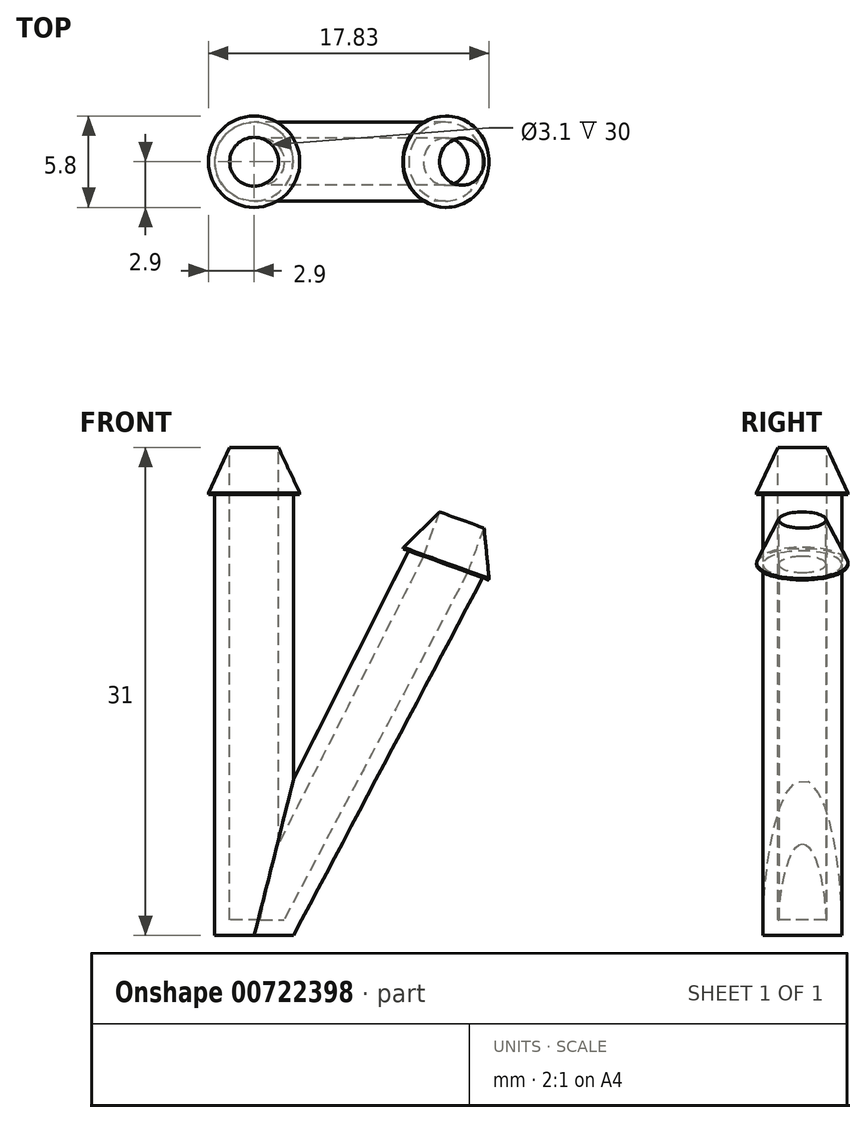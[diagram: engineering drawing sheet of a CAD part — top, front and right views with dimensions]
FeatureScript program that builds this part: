
annotation { "Feature Type Name" : "Feature", "Feature Type Description" : "" }
export const myFeature = defineFeature(function(context is Context, id is Id, definition is map)
    precondition{}
    {
        {
            var Q0;
            Q0=qCreatedBy(makeId("Top.planeOp"),FACE);
            var sketch = newSketch(context, id + "F0", { "sketchPlane" : qUnion([Q0])});
            skCircle(sketch, "E0", {"center": v(0, 0) * mm, "radius": 2.5 * mm});
            skSolve(sketch);
        }
        {
            var Q0;
            Q0=makeQuery(id+"F0.imprint","IMPRINT",FACE,{"disambiguationData":[TD([[makeQuery(id+"F0.imprint","IMPRINT",EDGE,{"derivedFrom":sQuery(id+"F0.wireOp",EDGE,"E0")}),1.0]])]});
            extrude(context, id + "F1", {"entities" : qUnion([Q0]), "depth" : 28 * mm, "offsetDistance" : 25 * mm});
        }
        {
            var Q0;
            Q0=makeQuery(id+"F1.opExtrude","CAP_FACE",FACE,{"disambiguationData":[OSD([sQuery(id+"F0.wireOp",EDGE,"E0")])],"isStart":false});
            var sketch = newSketch(context, id + "F2", { "sketchPlane" : qUnion([Q0])});
            skLineSegment(sketch, "E1", {"start": v(0, 2.5) * mm, "end": v(0, -2.5) * mm});
            skSolve(sketch);
        }
        {
            var Q0;
            Q0=sQuery(id+"F2.wireOp",EDGE,"E1");
            cPlane(context, id + "F3", {"entities" : qUnion([Q0]), "cplaneType" : CPlaneType.LINE_ANGLE, "offset" : 25 * mm, "angle" : 160 * degree, "width" : 150 * mm, "height" : 150 * mm});
        }
        {
            var Q0;
            Q0=qCreatedBy(id+"F3.planeOp",FACE);
            var sketch = newSketch(context, id + "F4", { "sketchPlane" : qUnion([Q0])});
            skCircle(sketch, "E2", {"center": v(3.37, 0) * mm, "radius": 2.5 * mm});
            skSolve(sketch);
        }
        {
            var Q1;
            Q1=makeQuery(id+"F4.imprint","IMPRINT",FACE,{"disambiguationData":[TD([[makeQuery(id+"F4.imprint","IMPRINT",EDGE,{"derivedFrom":sQuery(id+"F4.wireOp",EDGE,"E2")}),1.0]])]});
            var Q2;
            Q2=makeQuery(id+"F1.opExtrude","CAP_FACE",FACE,{"disambiguationData":[OSD([sQuery(id+"F0.wireOp",EDGE,"E0")])],"isStart":true});
            loft(context, id + "F5", {"operationType" : NewBodyOperationType.ADD, "sheetProfilesArray" : [{ "sheetProfileEntities" : qUnion([Q1]) }, { "sheetProfileEntities" : qUnion([Q2]) }]});
        }
        {
            var Q0;
            Q0=makeQuery(id+"F5.opLoft","CAP_FACE",FACE,{"disambiguationData":[OSD([makeQuery(id+"F4.imprint","IMPRINT",FACE,{"disambiguationData":[TD([[makeQuery(id+"F4.imprint","IMPRINT",EDGE,{"derivedFrom":sQuery(id+"F4.wireOp",EDGE,"E2")}),1.0]])]})])],"isStart":true});
            shell(context, id + "F6", {"entities" : qUnion([Q0]), "thickness" : 1 * mm});
        }
        {
            var Q0;
            Q0=makeQuery(id+"F1.opExtrude","CAP_FACE",FACE,{"disambiguationData":[OSD([sQuery(id+"F0.wireOp",EDGE,"E0")])],"isStart":false});
            var sketch = newSketch(context, id + "F7", { "sketchPlane" : qUnion([Q0])});
            skCircle(sketch, "E3", {"center": v(0, 0) * mm, "radius": 2.9 * mm});
            skSolve(sketch);
        }
        {
            var Q0;
            {var subQ0=sQuery(id+"F0.wireOp",EDGE,"E0");var subQ1=makeQuery(id+"F1.opExtrude","CAP_EDGE",EDGE,{"disambiguationData":[OSD([subQ0])],"isStart":false});Q0=makeQuery(id+"F7.imprint","IMPRINT",FACE,{"disambiguationData":[TD([[makeQuery(id+"F7.imprint","IMPRINT",EDGE,{"derivedFrom":subQ1}),1.0]])]});}
            cPlane(context, id + "F8", {"entities" : qUnion([Q0]), "cplaneType" : CPlaneType.OFFSET, "offset" : 3 * mm, "width" : 150 * mm, "height" : 150 * mm});
        }
        {
            var Q0;
            Q0=qCreatedBy(id+"F8.planeOp",FACE);
            var sketch = newSketch(context, id + "F9", { "sketchPlane" : qUnion([Q0])});
            skCircle(sketch, "E4", {"center": v(0, 0) * mm, "radius": 1.55 * mm});
            skSolve(sketch);
        }
        {
            var Q0;
            Q0=makeQuery(id+"F7.imprint","IMPRINT",FACE,{"disambiguationData":[TD([[makeQuery(id+"F7.imprint","IMPRINT",EDGE,{"derivedFrom":makeQuery(id+"F1.opExtrude","CAP_EDGE",EDGE,{"disambiguationData":[OSD([sQuery(id+"F0.wireOp",EDGE,"E0")])],"isStart":false})}),1.0]])]});
            var Q1;
            Q1=makeQuery(id+"F7.imprint","IMPRINT",FACE,{"disambiguationData":[TD([[makeQuery(id+"F7.imprint","IMPRINT",EDGE,{"derivedFrom":sQuery(id+"F7.wireOp",EDGE,"E3")}),1.0]])]});
            extrude(context, id + "F10", {"entities" : qUnion([Q0, Q1]), "operationType" : NewBodyOperationType.ADD, "depth" : .1 * mm, "offsetDistance" : 25 * mm});
        }
        {
            var Q1;
            Q1=makeQuery(id+"F10.opExtrude","CAP_FACE",FACE,{"disambiguationData":[OSD([sQuery(id+"F0.wireOp",EDGE,"E0"),sQuery(id+"F7.wireOp",EDGE,"E3")])],"isStart":false});
            var Q2;
            Q2=makeQuery(id+"F9.imprint","IMPRINT",FACE,{"disambiguationData":[TD([[makeQuery(id+"F9.imprint","IMPRINT",EDGE,{"derivedFrom":sQuery(id+"F9.wireOp",EDGE,"E4")}),1.0]])]});
            loft(context, id + "F11", {"operationType" : NewBodyOperationType.ADD, "sheetProfilesArray" : [{ "sheetProfileEntities" : qUnion([Q1]) }, { "sheetProfileEntities" : qUnion([Q2]) }]});
        }
        {
            var Q0;
            Q0=makeQuery(id+"F9.imprint","IMPRINT",FACE,{"disambiguationData":[TD([[makeQuery(id+"F9.imprint","IMPRINT",EDGE,{"derivedFrom":sQuery(id+"F9.wireOp",EDGE,"E4")}),1.0]])]});
            extrude(context, id + "F12", {"entities" : qUnion([Q0]), "operationType" : NewBodyOperationType.REMOVE, "oppositeDirection" : true, "depth" : 30 * mm, "offsetDistance" : 25 * mm});
        }
        {
            var Q0;
            Q0=makeQuery(id+"F5.opLoft","CAP_FACE",FACE,{"disambiguationData":[OSD([makeQuery(id+"F4.imprint","IMPRINT",FACE,{"disambiguationData":[TD([[makeQuery(id+"F4.imprint","IMPRINT",EDGE,{"derivedFrom":sQuery(id+"F4.wireOp",EDGE,"E2")}),1.0]])]})])],"isStart":true});
            cPlane(context, id + "F13", {"entities" : qUnion([Q0]), "cplaneType" : CPlaneType.OFFSET, "offset" : 3 * mm, "width" : 150 * mm, "height" : 150 * mm});
        }
        {
            var Q0;
            Q0=qCreatedBy(id+"F13.planeOp",FACE);
            var sketch = newSketch(context, id + "F14", { "sketchPlane" : qUnion([Q0])});
            skCircle(sketch, "E5", {"center": v(3.37, 0) * mm, "radius": 1.5 * mm});
            skSolve(sketch);
        }
        {
            var Q0;
            Q0=makeQuery(id+"F4.imprint","IMPRINT",FACE,{"disambiguationData":[TD([[makeQuery(id+"F4.imprint","IMPRINT",EDGE,{"derivedFrom":sQuery(id+"F4.wireOp",EDGE,"E2")}),1.0]])]});
            var sketch = newSketch(context, id + "F15", { "sketchPlane" : qUnion([Q0])});
            skCircle(sketch, "E6", {"center": v(3.37, 0) * mm, "radius": 2.9 * mm});
            skSolve(sketch);
        }
        {
            var Q0;
            Q0=makeQuery(id+"F15.imprint","IMPRINT",FACE,{"disambiguationData":[TD([[makeQuery(id+"F15.imprint","IMPRINT",EDGE,{"derivedFrom":makeQuery(id+"F4.imprint","IMPRINT",EDGE,{"derivedFrom":sQuery(id+"F4.wireOp",EDGE,"E2")})}),1.0]])]});
            var Q1;
            Q1=makeQuery(id+"F15.imprint","IMPRINT",FACE,{"disambiguationData":[TD([[makeQuery(id+"F15.imprint","IMPRINT",EDGE,{"derivedFrom":sQuery(id+"F15.wireOp",EDGE,"E6")}),1.0]])]});
            extrude(context, id + "F16", {"entities" : qUnion([Q0, Q1]), "operationType" : NewBodyOperationType.ADD, "depth" : .1 * mm, "offsetDistance" : 25 * mm});
        }
        {
            var Q1;
            Q1=makeQuery(id+"F14.imprint","IMPRINT",FACE,{"disambiguationData":[TD([[makeQuery(id+"F14.imprint","IMPRINT",EDGE,{"derivedFrom":sQuery(id+"F14.wireOp",EDGE,"E5")}),1.0]])]});
            var Q2;
            Q2=makeQuery(id+"F16.opExtrude","CAP_FACE",FACE,{"disambiguationData":[OSD([sQuery(id+"F15.wireOp",EDGE,"E6")])],"isStart":false});
            loft(context, id + "F17", {"operationType" : NewBodyOperationType.ADD, "sheetProfilesArray" : [{ "sheetProfileEntities" : qUnion([Q1]) }, { "sheetProfileEntities" : qUnion([Q2]) }]});
        }
        {
            var Q0;
            Q0=makeQuery(id+"F14.imprint","IMPRINT",FACE,{"disambiguationData":[TD([[makeQuery(id+"F14.imprint","IMPRINT",EDGE,{"derivedFrom":sQuery(id+"F14.wireOp",EDGE,"E5")}),1.0]])]});
            extrude(context, id + "F18", {"entities" : qUnion([Q0]), "operationType" : NewBodyOperationType.REMOVE, "oppositeDirection" : true, "depth" : 3 * mm, "offsetDistance" : 25 * mm});
        }
    });
